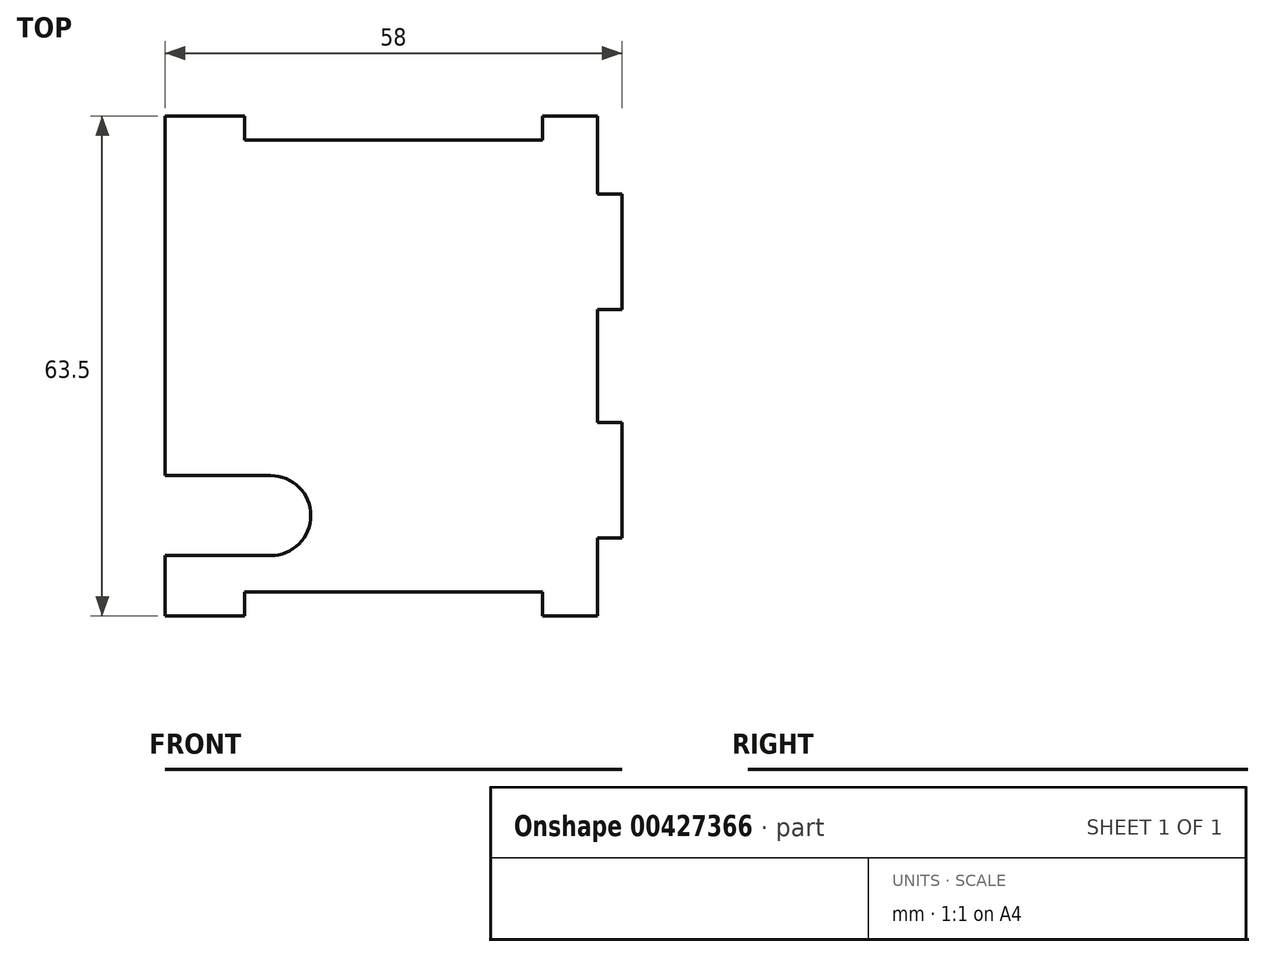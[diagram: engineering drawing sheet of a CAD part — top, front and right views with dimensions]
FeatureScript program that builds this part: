
annotation { "Feature Type Name" : "Feature", "Feature Type Description" : "" }
export const myFeature = defineFeature(function(context is Context, id is Id, definition is map)
    precondition{}
    {
        {
            var Q0;
            Q0=qCreatedBy(makeId("Top.planeOp"),FACE);
            var sketch = newSketch(context, id + "F0", { "sketchPlane" : qUnion([Q0])});
            skLineSegment(sketch, "E0.bottom", {"start": v(29, 31.75) * mm, "end": v(-29, 31.75) * mm});
            skLineSegment(sketch, "E0.top", {"start": v(29, -31.75) * mm, "end": v(-29, -31.75) * mm});
            skLineSegment(sketch, "E0.left", {"start": v(29, 31.75) * mm, "end": v(29, -31.75) * mm});
            skLineSegment(sketch, "E0.right", {"start": v(-29, 31.75) * mm, "end": v(-29, -31.75) * mm});
            skPoint(sketch, "E0.middle", {"position": v(0, 0) * mm});
            skSolve(sketch);
        }
        {
            var Q0;
            Q0=makeQuery(id+"F0.imprint","IMPRINT",FACE,{"disambiguationData":[TD([[makeQuery(id+"F0.imprint","IMPRINT",EDGE,{"derivedFrom":sQuery(id+"F0.wireOp",EDGE,"E0.bottom")}),1.0]])]});
            extrude(context, id + "F1", {"entities" : qUnion([Q0]), "depth" : 1 / 203.2 * mm, "offsetDistance" : 25 * mm});
        }
        {
            var Q0;
            Q0=makeQuery(id+"F1.opExtrude","CAP_FACE",FACE,{"disambiguationData":[OSD([sQuery(id+"F0.wireOp",EDGE,"E0.bottom"),sQuery(id+"F0.wireOp",EDGE,"E0.top"),sQuery(id+"F0.wireOp",EDGE,"E0.left"),sQuery(id+"F0.wireOp",EDGE,"E0.right")])],"isStart":false});
            var sketch = newSketch(context, id + "F2", { "sketchPlane" : qUnion([Q0])});
            skLineSegment(sketch, "E1.bottom", {"start": v(-29, 31.75) * mm, "end": v(29, 31.75) * mm, "construction": true});
            skLineSegment(sketch, "E1.top", {"start": v(-29, -31.75) * mm, "end": v(29, -31.75) * mm, "construction": true});
            skLineSegment(sketch, "E1.left", {"start": v(-29, 31.75) * mm, "end": v(-29, -31.75) * mm, "construction": true});
            skLineSegment(sketch, "E1.right", {"start": v(29, 31.75) * mm, "end": v(29, -31.75) * mm, "construction": true});
            skLineSegment(sketch, "E2", {"start": v(-25.93, 31.75) * mm, "end": v(-25.93, -31.75) * mm, "construction": true});
            skLineSegment(sketch, "E3", {"start": v(25.93, 31.75) * mm, "end": v(25.93, -31.75) * mm, "construction": true});
            skLineSegment(sketch, "E4", {"start": v(-29, -28.68) * mm, "end": v(29, -28.67) * mm, "construction": true});
            skLineSegment(sketch, "E5", {"start": v(-29, 28.67) * mm, "end": v(29, 28.68) * mm, "construction": true});
            skLineSegment(sketch, "E6.0", {"start": v(-19, 31.75) * mm, "end": v(-19, -31.75) * mm, "construction": true});
            skLineSegment(sketch, "E7.0", {"start": v(19, 31.75) * mm, "end": v(19, -31.75) * mm, "construction": true});
            skLineSegment(sketch, "E8.0", {"start": v(-29, -21.75) * mm, "end": v(29, -21.75) * mm, "construction": true});
            skLineSegment(sketch, "E9.0", {"start": v(-29, 21.75) * mm, "end": v(29, 21.75) * mm, "construction": true});
            skLineSegment(sketch, "E10.bottom", {"start": v(18.9, 31.75) * mm, "end": v(-18.9, 31.75) * mm});
            skLineSegment(sketch, "E10.top", {"start": v(18.9, 28.67) * mm, "end": v(-18.9, 28.67) * mm});
            skLineSegment(sketch, "E10.left", {"start": v(18.9, 31.75) * mm, "end": v(18.9, 28.68) * mm});
            skLineSegment(sketch, "E10.right", {"start": v(-18.9, 31.75) * mm, "end": v(-18.9, 28.67) * mm});
            skLineSegment(sketch, "E11.bottom", {"start": v(18.9, -28.67) * mm, "end": v(-18.9, -28.67) * mm});
            skLineSegment(sketch, "E11.top", {"start": v(18.9, -31.75) * mm, "end": v(-18.9, -31.75) * mm});
            skLineSegment(sketch, "E11.left", {"start": v(18.9, -28.67) * mm, "end": v(18.9, -31.75) * mm});
            skLineSegment(sketch, "E11.right", {"start": v(-18.9, -28.68) * mm, "end": v(-18.9, -31.75) * mm});
            skLineSegment(sketch, "E12", {"start": v(25.93, 7.25) * mm, "end": v(29, 7.25) * mm, "construction": true});
            skLineSegment(sketch, "E13", {"start": v(25.93, -7.25) * mm, "end": v(29, -7.25) * mm, "construction": true});
            skLineSegment(sketch, "E14", {"start": v(27.46, -7.25) * mm, "end": v(27.46, -21.75) * mm, "construction": true});
            skLineSegment(sketch, "E15", {"start": v(27.46, -7.25) * mm, "end": v(27.46, 7.25) * mm, "construction": true});
            skLineSegment(sketch, "E16", {"start": v(27.46, 7.25) * mm, "end": v(27.46, 21.75) * mm, "construction": true});
            skLineSegment(sketch, "E17.bottom", {"start": v(29, -7.15) * mm, "end": v(25.93, -7.15) * mm});
            skLineSegment(sketch, "E17.top", {"start": v(29, 7.15) * mm, "end": v(25.93, 7.15) * mm});
            skLineSegment(sketch, "E17.left", {"start": v(29, -7.15) * mm, "end": v(29, 7.15) * mm});
            skLineSegment(sketch, "E17.right", {"start": v(25.93, -7.15) * mm, "end": v(25.93, 7.15) * mm});
            skLineSegment(sketch, "E18.bottom", {"start": v(29, 21.85) * mm, "end": v(25.93, 21.85) * mm});
            skLineSegment(sketch, "E18.top", {"start": v(29, 31.75) * mm, "end": v(25.92, 31.75) * mm});
            skLineSegment(sketch, "E18.left", {"start": v(29, 21.85) * mm, "end": v(29, 31.75) * mm});
            skLineSegment(sketch, "E18.right", {"start": v(25.93, 21.85) * mm, "end": v(25.93, 31.75) * mm});
            skLineSegment(sketch, "E19.bottom", {"start": v(29, -31.75) * mm, "end": v(25.93, -31.75) * mm});
            skLineSegment(sketch, "E19.top", {"start": v(29, -21.85) * mm, "end": v(25.93, -21.85) * mm});
            skLineSegment(sketch, "E19.left", {"start": v(29, -31.75) * mm, "end": v(29, -21.85) * mm});
            skLineSegment(sketch, "E19.right", {"start": v(25.93, -31.75) * mm, "end": v(25.93, -21.85) * mm});
            skSolve(sketch);
        }
        {
            var Q0;
            Q0=makeQuery(id+"F2.imprint","IMPRINT",FACE,{"disambiguationData":[TD([[makeQuery(id+"F2.imprint","IMPRINT",EDGE,{"derivedFrom":sQuery(id+"F2.wireOp",EDGE,"E11.bottom")}),1.0]])]});
            var Q1;
            Q1=makeQuery(id+"F2.imprint","IMPRINT",FACE,{"disambiguationData":[TD([[makeQuery(id+"F2.imprint","IMPRINT",EDGE,{"derivedFrom":sQuery(id+"F2.wireOp",EDGE,"E10.bottom")}),1.0]])]});
            var Q2;
            Q2=makeQuery(id+"F2.imprint","IMPRINT",FACE,{"disambiguationData":[TD([[makeQuery(id+"F2.imprint","IMPRINT",EDGE,{"derivedFrom":sQuery(id+"F2.wireOp",EDGE,"E17.bottom")}),-1.0]])]});
            var Q3;
            Q3=makeQuery(id+"F2.imprint","IMPRINT",FACE,{"disambiguationData":[TD([[makeQuery(id+"F2.imprint","IMPRINT",EDGE,{"derivedFrom":sQuery(id+"F2.wireOp",EDGE,"E19.bottom")}),-1.0]])]});
            var Q4;
            Q4=makeQuery(id+"F2.imprint","IMPRINT",FACE,{"disambiguationData":[TD([[makeQuery(id+"F2.imprint","IMPRINT",EDGE,{"derivedFrom":sQuery(id+"F2.wireOp",EDGE,"E18.bottom")}),-1.0]])]});
            extrude(context, id + "F3", {"entities" : qUnion([Q0, Q1, Q2, Q3, Q4]), "operationType" : NewBodyOperationType.REMOVE, "oppositeDirection" : true, "depth" : 25 * mm, "offsetDistance" : 25 * mm});
        }
        {
            var Q0;
            Q0=makeQuery(id+"F1.opExtrude","CAP_FACE",FACE,{"disambiguationData":[OSD([sQuery(id+"F0.wireOp",EDGE,"E0.bottom"),sQuery(id+"F0.wireOp",EDGE,"E0.top"),sQuery(id+"F0.wireOp",EDGE,"E0.left"),sQuery(id+"F0.wireOp",EDGE,"E0.right")])],"isStart":false});
            var sketch = newSketch(context, id + "F4", { "sketchPlane" : qUnion([Q0])});
            skLineSegment(sketch, "E20", {"start": v(-15.6, -19) * mm, "end": v(-29, -19) * mm, "construction": true});
            skCircle(sketch, "E21", {"center": v(-15.6, -19) * mm, "radius": 5.08 * mm});
            skLineSegment(sketch, "E22", {"start": v(-15.6, -24.08) * mm, "end": v(-29, -24.08) * mm});
            skLineSegment(sketch, "E23", {"start": v(-15.6, -13.92) * mm, "end": v(-29, -13.92) * mm});
            skSolve(sketch);
        }
        {
            var Q0;
            {var subQ0=sQuery(id+"F4.wireOp",EDGE,"E22");Q0=makeQuery(id+"F4.imprint","IMPRINT",FACE,{"disambiguationData":[TD([[makeQuery(id+"F4.imprint","IMPRINT",EDGE,{"derivedFrom":subQ0}),-1.0]])]});}
            var Q1;
            {var subQ0=sQuery(id+"F4.wireOp",EDGE,"E21");var subQ1=makeQuery(id+"F4.imprint","INTERSECT",VERTEX,{"derivedFrom":[subQ0,sQuery(id+"F4.wireOp",EDGE,"E22")]});Q1=makeQuery(id+"F4.imprint","IMPRINT",FACE,{"disambiguationData":[TD([[makeQuery(id+"F4.imprint","IMPRINT",EDGE,{"disambiguationData":[TD([[subQ1,1.0]])],"derivedFrom":subQ0}),1.0]])]});}
            extrude(context, id + "F5", {"entities" : qUnion([Q0, Q1]), "operationType" : NewBodyOperationType.REMOVE, "oppositeDirection" : true, "depth" : 25 * mm, "offsetDistance" : 25 * mm});
        }
    });
